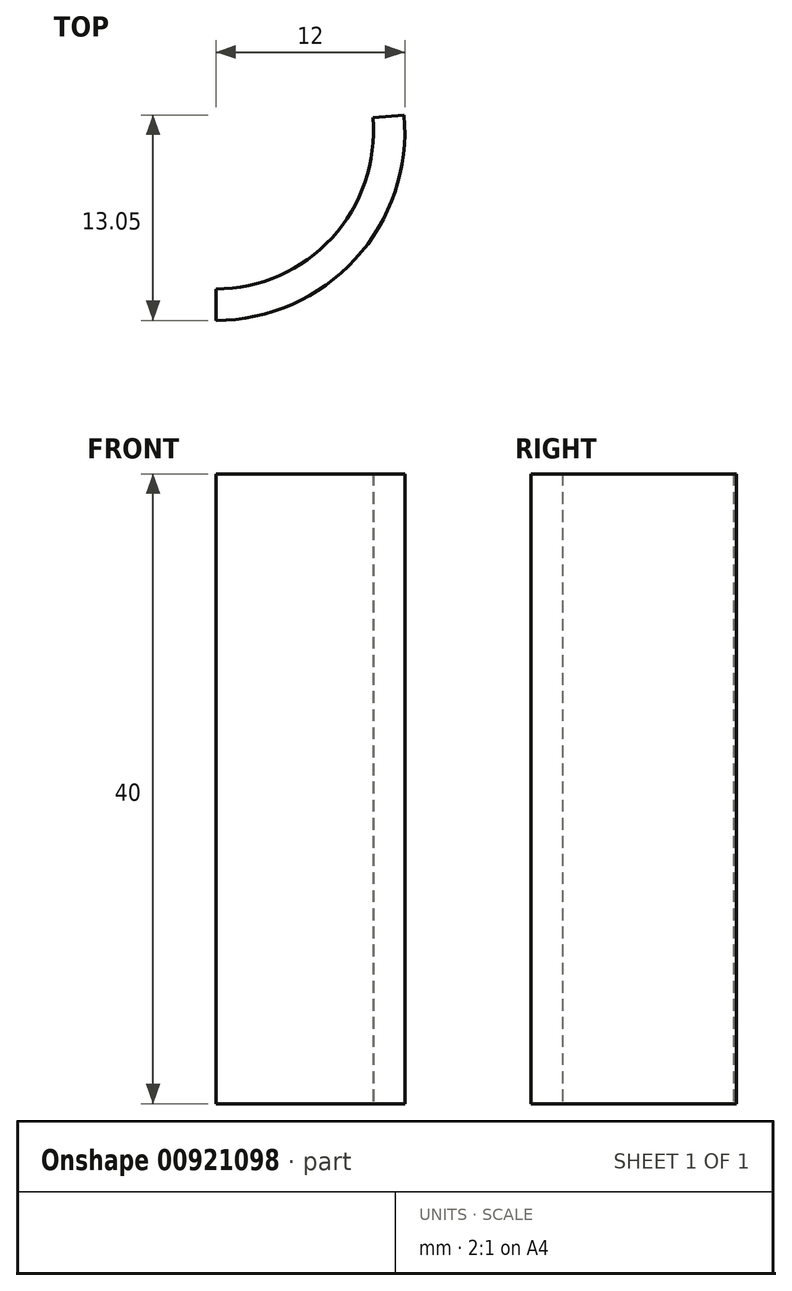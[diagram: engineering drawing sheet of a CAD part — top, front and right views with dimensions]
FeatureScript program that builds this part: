
annotation { "Feature Type Name" : "Feature", "Feature Type Description" : "" }
export const myFeature = defineFeature(function(context is Context, id is Id, definition is map)
    precondition{}
    {
        {
            var Q0;
            Q0=qCreatedBy(makeId("Top.planeOp"),FACE);
            var sketch = newSketch(context, id + "F0", { "sketchPlane" : qUnion([Q0])});
            skLineSegment(sketch, "E0", {"start": v(0, 0) * mm, "end": v(0, -10) * mm});
            skLineSegment(sketch, "E1", {"start": v(0, 0) * mm, "end": v(9.96, 0.87) * mm});
            skArc(sketch, "E2", {"start": v(0, -10) * mm, "mid": v(7.37, -6.76) * mm, "end": v(9.96, 0.87) * mm});
            skArc(sketch, "E3", {"start": v(0, -12) * mm, "mid": v(8.85, -8.1) * mm, "end": v(11.95, 1.05) * mm});
            skLineSegment(sketch, "E4", {"start": v(0, -10) * mm, "end": v(0, -12) * mm});
            skLineSegment(sketch, "E5", {"start": v(9.96, 0.87) * mm, "end": v(11.95, 1.05) * mm});
            skSolve(sketch);
        }
        {
            var Q0;
            Q0=makeQuery(id+"F0.imprint","IMPRINT",FACE,{"disambiguationData":[TD([[makeQuery(id+"F0.imprint","IMPRINT",EDGE,{"derivedFrom":sQuery(id+"F0.wireOp",EDGE,"E2")}),-1.0]])]});
            extrude(context, id + "F1", {"entities" : qUnion([Q0]), "depth" : 40 * mm, "offsetDistance" : 25 * mm});
        }
    });
